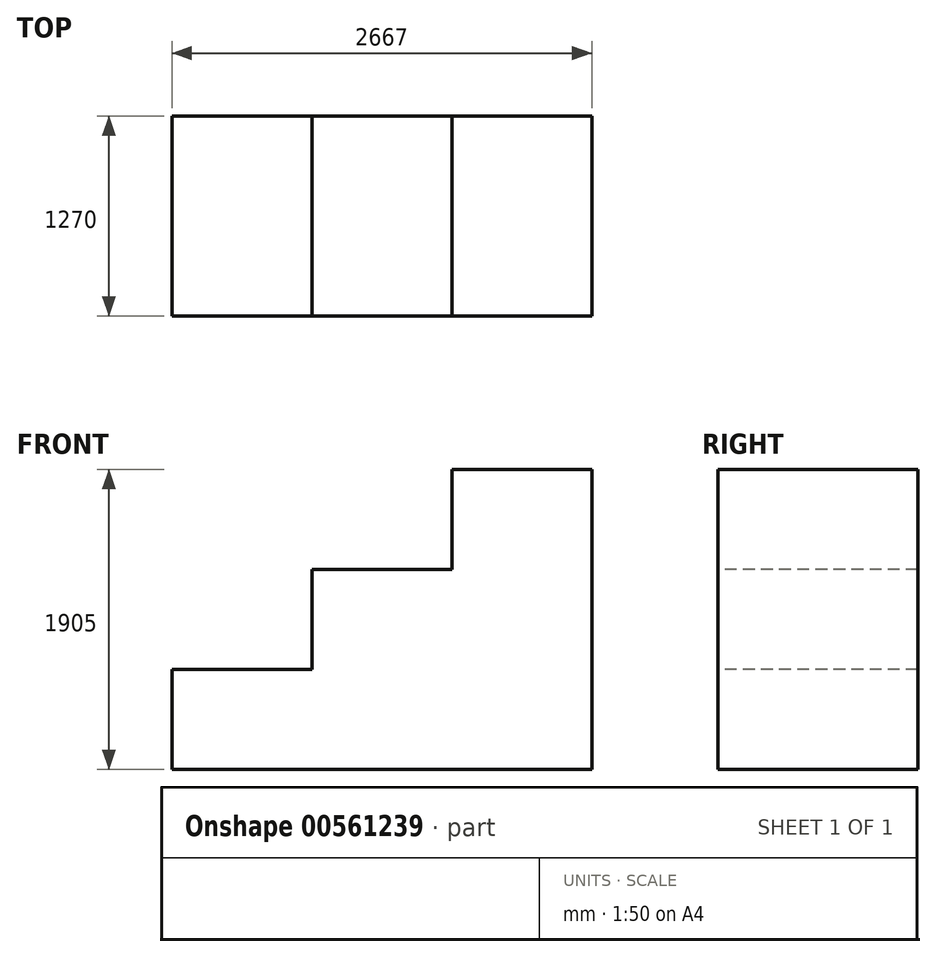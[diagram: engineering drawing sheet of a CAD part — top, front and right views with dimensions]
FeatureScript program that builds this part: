
annotation { "Feature Type Name" : "Feature", "Feature Type Description" : "" }
export const myFeature = defineFeature(function(context is Context, id is Id, definition is map)
    precondition{}
    {
        {
            var Q0;
            Q0=qCreatedBy(makeId("Front.planeOp"),FACE);
            var sketch = newSketch(context, id + "F0", { "sketchPlane" : qUnion([Q0])});
            skLineSegment(sketch, "E0.bottom", {"start": v(0, 0) * mm, "end": v(2667, 0) * mm});
            skLineSegment(sketch, "E0.top", {"start": v(0, 1905) * mm, "end": v(2667, 1905) * mm});
            skLineSegment(sketch, "E0.left", {"start": v(0, 0) * mm, "end": v(0, 1905) * mm});
            skLineSegment(sketch, "E0.right", {"start": v(2667, 0) * mm, "end": v(2667, 1905) * mm});
            skSolve(sketch);
        }
        {
            var Q0;
            Q0 = qSketchRegion(id + "F0", true);
            extrude(context, id + "F1", {"entities" : qUnion([Q0]), "depth" : 1270 * mm, "offsetDistance" : 25.4 * mm});
        }
        {
            var Q0;
            Q0=makeQuery(id+"F1.opExtrude","CAP_FACE",FACE,{"disambiguationData":[OSD([sQuery(id+"F0.wireOp",EDGE,"E0.bottom"),sQuery(id+"F0.wireOp",EDGE,"E0.top"),sQuery(id+"F0.wireOp",EDGE,"E0.left"),sQuery(id+"F0.wireOp",EDGE,"E0.right")])],"isStart":false});
            var sketch = newSketch(context, id + "F2", { "sketchPlane" : qUnion([Q0])});
            skLineSegment(sketch, "E1", {"start": v(0, 635) * mm, "end": v(889, 635) * mm});
            skLineSegment(sketch, "E2", {"start": v(889, 635) * mm, "end": v(889, 1270) * mm});
            skLineSegment(sketch, "E3", {"start": v(889, 1270) * mm, "end": v(1778, 1270) * mm});
            skLineSegment(sketch, "E4", {"start": v(1778, 1270) * mm, "end": v(1778, 1905) * mm});
            skSolve(sketch);
        }
        {
            var Q0;
            {var subQ1=sQuery(id+"F2.wireOp",EDGE,"E1");Q0=makeQuery(id+"F2.imprint","IMPRINT",FACE,{"disambiguationData":[TD([[makeQuery(id+"F2.imprint","IMPRINT",EDGE,{"derivedFrom":subQ1}),1.0]])]});}
            var sketch = newSketch(context, id + "F3", { "sketchPlane" : qUnion([Q0])});
            skSolve(sketch);
        }
        {
            var Q0;
            Q0 = qSketchRegion(id + "F3", true);
            var Q1;
            {var subQ1=sQuery(id+"F2.wireOp",EDGE,"E1");Q1=makeQuery(id+"F2.imprint","IMPRINT",FACE,{"disambiguationData":[TD([[makeQuery(id+"F2.imprint","IMPRINT",EDGE,{"derivedFrom":subQ1}),1.0]])]});}
            extrude(context, id + "F4", {"entities" : qUnion([Q0, Q1]), "operationType" : NewBodyOperationType.REMOVE, "oppositeDirection" : true, "depth" : 1270 * mm, "offsetDistance" : 25.4 * mm});
        }
    });
